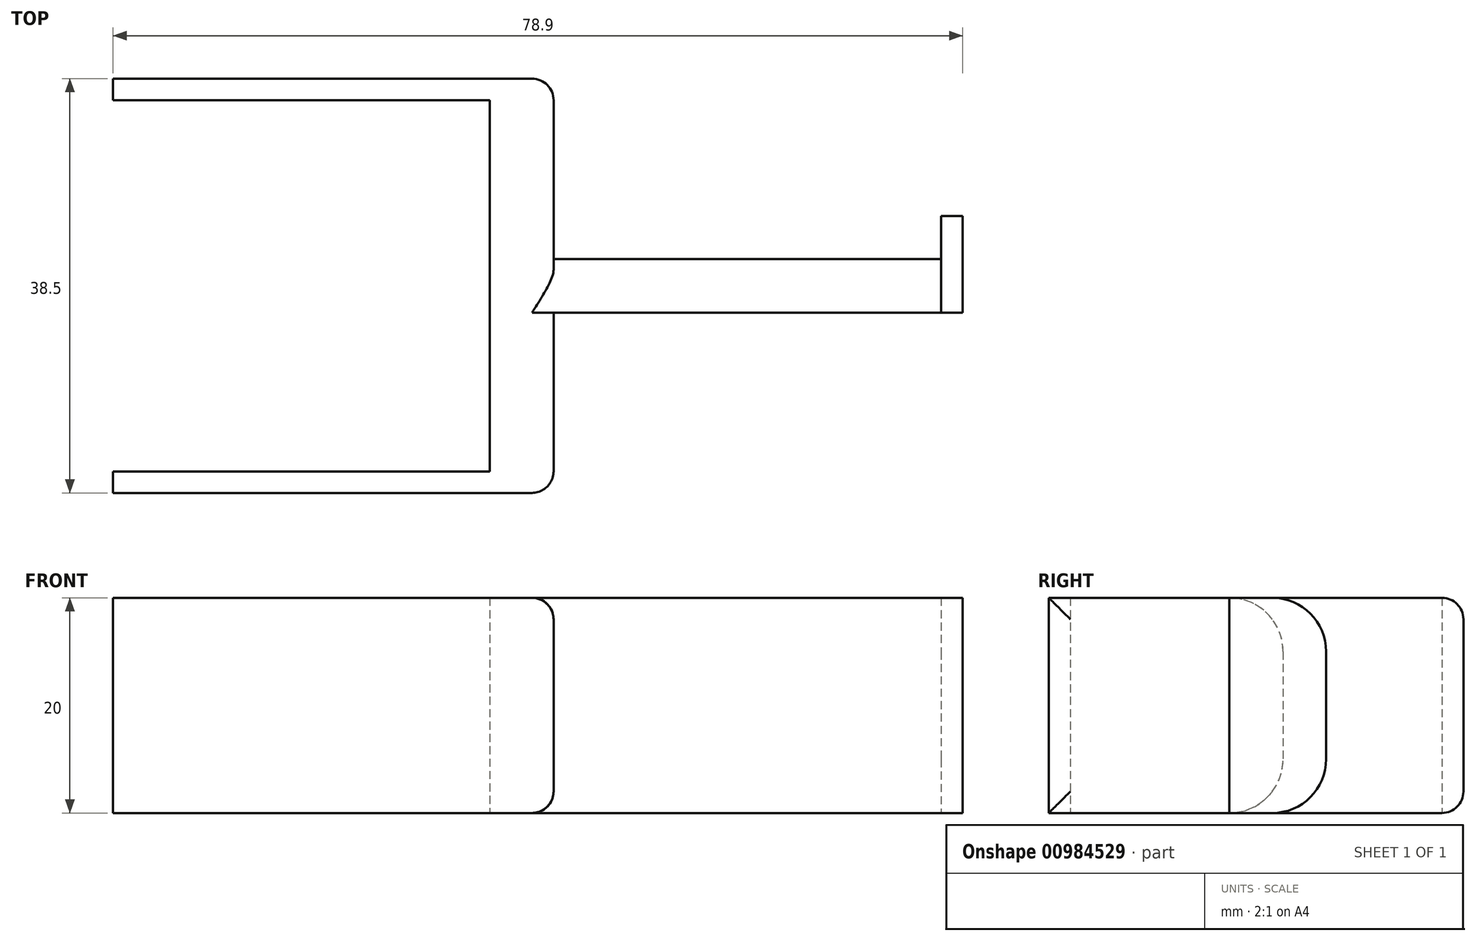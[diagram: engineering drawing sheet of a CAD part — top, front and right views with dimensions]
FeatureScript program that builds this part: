
annotation { "Feature Type Name" : "Feature", "Feature Type Description" : "" }
export const myFeature = defineFeature(function(context is Context, id is Id, definition is map)
    precondition{}
    {
        {
            var Q0;
            Q0=qCreatedBy(makeId("Top.planeOp"),FACE);
            var sketch = newSketch(context, id + "F0", { "sketchPlane" : qUnion([Q0])});
            skLineSegment(sketch, "E0.bottom", {"start": v(2.95, 19.25) * mm, "end": v(-2.95, 19.25) * mm});
            skLineSegment(sketch, "E0.top", {"start": v(2.95, -19.25) * mm, "end": v(-2.95, -19.25) * mm});
            skLineSegment(sketch, "E0.left", {"start": v(2.95, 19.25) * mm, "end": v(2.95, -19.25) * mm});
            skLineSegment(sketch, "E0.right", {"start": v(-2.95, 19.25) * mm, "end": v(-2.95, -19.25) * mm});
            skPoint(sketch, "E0.middle", {"position": v(0, 0) * mm});
            skLineSegment(sketch, "E1.bottom", {"start": v(-2.95, 19.25) * mm, "end": v(-37.95, 19.25) * mm});
            skLineSegment(sketch, "E1.top", {"start": v(-2.95, 17.25) * mm, "end": v(-37.95, 17.25) * mm});
            skLineSegment(sketch, "E1.left", {"start": v(-2.95, 19.25) * mm, "end": v(-2.95, 17.25) * mm});
            skLineSegment(sketch, "E1.right", {"start": v(-37.95, 19.25) * mm, "end": v(-37.95, 17.25) * mm});
            skLineSegment(sketch, "E2.bottom", {"start": v(-2.95, -19.25) * mm, "end": v(-37.95, -19.25) * mm});
            skLineSegment(sketch, "E2.top", {"start": v(-2.95, -17.25) * mm, "end": v(-37.95, -17.25) * mm});
            skLineSegment(sketch, "E2.left", {"start": v(-2.95, -19.25) * mm, "end": v(-2.95, -17.25) * mm});
            skLineSegment(sketch, "E2.right", {"start": v(-37.95, -19.25) * mm, "end": v(-37.95, -17.25) * mm});
            skLineSegment(sketch, "E3", {"start": v(2.95, 2.5) * mm, "end": v(40.95, 2.5) * mm});
            skLineSegment(sketch, "E4", {"start": v(2.95, -2.5) * mm, "end": v(40.95, -2.5) * mm});
            skPoint(sketch, "E5", {"position": v(2.95, 0) * mm});
            skLineSegment(sketch, "E6", {"start": v(40.95, 2.5) * mm, "end": v(40.95, -2.5) * mm});
            skLineSegment(sketch, "E7.bottom", {"start": v(40.95, 2.5) * mm, "end": v(38.95, 2.5) * mm});
            skLineSegment(sketch, "E7.top", {"start": v(40.95, 6.5) * mm, "end": v(38.95, 6.5) * mm});
            skLineSegment(sketch, "E7.left", {"start": v(40.95, 2.5) * mm, "end": v(40.95, 6.5) * mm});
            skLineSegment(sketch, "E7.right", {"start": v(38.95, 2.5) * mm, "end": v(38.95, 6.5) * mm});
            skSolve(sketch);
        }
        {
            var Q0;
            {var subQ0=sQuery(id+"F0.wireOp",EDGE,"E1.bottom");Q0=makeQuery(id+"F0.imprint","IMPRINT",FACE,{"disambiguationData":[TD([[makeQuery(id+"F0.imprint","IMPRINT",EDGE,{"derivedFrom":subQ0}),1.0]])]});}
            var Q1;
            {var subQ1=sQuery(id+"F0.wireOp",EDGE,"E0.bottom");Q1=makeQuery(id+"F0.imprint","IMPRINT",FACE,{"disambiguationData":[TD([[makeQuery(id+"F0.imprint","IMPRINT",EDGE,{"derivedFrom":subQ1}),1.0]])]});}
            var Q2;
            {var subQ0=sQuery(id+"F0.wireOp",EDGE,"E4");Q2=makeQuery(id+"F0.imprint","IMPRINT",FACE,{"disambiguationData":[TD([[makeQuery(id+"F0.imprint","IMPRINT",EDGE,{"derivedFrom":subQ0}),1.0]])]});}
            var Q3;
            Q3=makeQuery(id+"F0.imprint","IMPRINT",FACE,{"disambiguationData":[TD([[makeQuery(id+"F0.imprint","IMPRINT",EDGE,{"derivedFrom":sQuery(id+"F0.wireOp",EDGE,"E7.top")}),1.0]])]});
            var Q4;
            {var subQ0=sQuery(id+"F0.wireOp",EDGE,"E2.bottom");Q4=makeQuery(id+"F0.imprint","IMPRINT",FACE,{"disambiguationData":[TD([[makeQuery(id+"F0.imprint","IMPRINT",EDGE,{"derivedFrom":subQ0}),-1.0]])]});}
            extrude(context, id + "F1", {"entities" : qUnion([Q0, Q1, Q2, Q3, Q4]), "depth" : 20 * mm, "offsetDistance" : 25 * mm});
        }
        {
            var Q0;
            Q0=makeQuery(id+"F1.opExtrude","CAP_EDGE",EDGE,{"disambiguationData":[OSD([sQuery(id+"F0.wireOp",EDGE,"E3")])],"isStart":false});
            var Q1;
            Q1=makeQuery(id+"F1.opExtrude","CAP_EDGE",EDGE,{"disambiguationData":[OSD([sQuery(id+"F0.wireOp",EDGE,"E3")])],"isStart":true});
            fillet(context, id + "F2", {"entities" : qUnion([Q0, Q1]), "radius" : 5 * mm, "tangentPropagation" : true, "allowEdgeOverflow" : false});
        }
        {
            var Q0;
            Q0=makeQuery(id+"F1.opExtrude","CAP_EDGE",EDGE,{"disambiguationData":[OSD([sQuery(id+"F0.wireOp",EDGE,"E7.top")])],"isStart":false});
            var Q1;
            Q1=makeQuery(id+"F1.opExtrude","CAP_EDGE",EDGE,{"disambiguationData":[OSD([sQuery(id+"F0.wireOp",EDGE,"E7.top")])],"isStart":true});
            fillet(context, id + "F3", {"entities" : qUnion([Q0, Q1]), "radius" : 5 * mm, "tangentPropagation" : true, "allowEdgeOverflow" : false});
        }
        {
            var Q0;
            {var subQ0=sQuery(id+"F0.wireOp",EDGE,"E0.left");Q0=makeQuery(id+"F1.opExtrude","CAP_EDGE",EDGE,{"disambiguationData":[OSD([subQ0]),TDD([makeQuery(id+"F0.imprint","IMPRINT",EDGE,{"disambiguationData":[TD([[makeQuery(id+"F0.imprint","INTERSECT",VERTEX,{"derivedFrom":[sQuery(id+"F0.wireOp",EDGE,"E0.bottom"),subQ0]}),-1.0]])],"derivedFrom":subQ0})])],"isStart":false});}
            var Q1;
            {var subQ0=sQuery(id+"F0.wireOp",EDGE,"E0.left");Q1=makeQuery(id+"F1.opExtrude","CAP_EDGE",EDGE,{"disambiguationData":[OSD([subQ0]),TDD([makeQuery(id+"F0.imprint","IMPRINT",EDGE,{"disambiguationData":[TD([[makeQuery(id+"F0.imprint","INTERSECT",VERTEX,{"derivedFrom":[sQuery(id+"F0.wireOp",EDGE,"E0.top"),subQ0]}),1.0]])],"derivedFrom":subQ0})])],"isStart":false});}
            var Q2;
            {var subQ0=sQuery(id+"F0.wireOp",EDGE,"E0.left");Q2=makeQuery(id+"F1.opExtrude","CAP_EDGE",EDGE,{"disambiguationData":[OSD([subQ0]),TDD([makeQuery(id+"F0.imprint","IMPRINT",EDGE,{"disambiguationData":[TD([[makeQuery(id+"F0.imprint","INTERSECT",VERTEX,{"derivedFrom":[sQuery(id+"F0.wireOp",EDGE,"E0.bottom"),subQ0]}),-1.0]])],"derivedFrom":subQ0})])],"isStart":true});}
            var Q3;
            {var subQ0=sQuery(id+"F0.wireOp",EDGE,"E0.left");Q3=makeQuery(id+"F1.opExtrude","CAP_EDGE",EDGE,{"disambiguationData":[OSD([subQ0]),TDD([makeQuery(id+"F0.imprint","IMPRINT",EDGE,{"disambiguationData":[TD([[makeQuery(id+"F0.imprint","INTERSECT",VERTEX,{"derivedFrom":[sQuery(id+"F0.wireOp",EDGE,"E0.top"),subQ0]}),1.0]])],"derivedFrom":subQ0})])],"isStart":true});}
            var Q4;
            Q4=makeQuery(id+"F1.opExtrude","SWEPT_EDGE",EDGE,{"disambiguationData":[OSD([sQuery(id+"F0.wireOp",EDGE,"E0.bottom"),sQuery(id+"F0.wireOp",EDGE,"E0.left")])]});
            var Q5;
            Q5=makeQuery(id+"F1.opExtrude","SWEPT_EDGE",EDGE,{"disambiguationData":[OSD([sQuery(id+"F0.wireOp",EDGE,"E0.top"),sQuery(id+"F0.wireOp",EDGE,"E0.left")])]});
            fillet(context, id + "F4", {"entities" : qUnion([Q0, Q1, Q2, Q3, Q4, Q5]), "radius" : 2 * mm, "tangentPropagation" : true, "allowEdgeOverflow" : false});
        }
        {
            var Q0;
            Q0=makeQuery(id+"F1.opExtrude","CAP_EDGE",EDGE,{"disambiguationData":[OSD([sQuery(id+"F0.wireOp",EDGE,"E0.bottom"),sQuery(id+"F0.wireOp",EDGE,"E1.bottom")])],"isStart":true});
            var Q1;
            Q1=makeQuery(id+"F1.opExtrude","CAP_EDGE",EDGE,{"disambiguationData":[OSD([sQuery(id+"F0.wireOp",EDGE,"E0.bottom"),sQuery(id+"F0.wireOp",EDGE,"E1.bottom")])],"isStart":false});
            fillet(context, id + "F5", {"entities" : qUnion([Q0, Q1]), "radius" : 2 * mm, "tangentPropagation" : true, "allowEdgeOverflow" : false});
        }
    });
